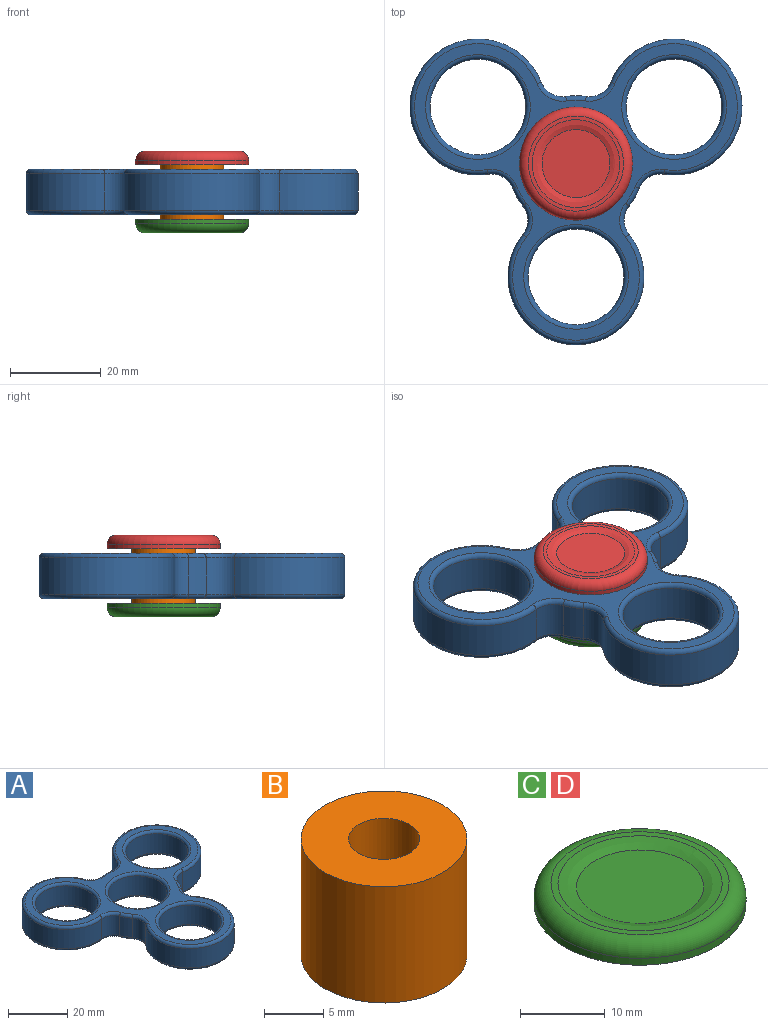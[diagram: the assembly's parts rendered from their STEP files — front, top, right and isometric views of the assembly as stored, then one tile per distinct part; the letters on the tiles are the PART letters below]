
ASSEMBLY  parts=4 mates=3
PART A: 50 faces, bbox 75.8x70x10 mm
  f0: cylinder r=15mm len=8mm, axis (0,0,-1), area 36.4mm2, adj f12,f17,f28,f39
  f1: cylinder r=15mm len=30mm, axis (0,0,-1), area 539mm2, adj f12,f13,f24,f35
  f2: cylinder r=15mm len=8mm, axis (0,0,-1), area 36.4mm2, adj f13,f14,f20,f31
  f3: cylinder r=15mm len=30mm, axis (0,0,-1), area 539mm2, adj f14,f15,f19,f32
  f4: cylinder r=15mm len=8mm, axis (0,0,-1), area 36.4mm2, adj f15,f16,f23,f36
  f5: cylinder r=10.56mm len=21.12mm, axis (0,0,-1), area 530.8mm2, adj f43,f48
  f6: cylinder r=10mm len=20mm, axis (0,0,-1), area 502.7mm2, adj f44,f47
  f7: cylinder r=15mm len=30mm, axis (0,0,-1), area 539mm2, adj f16,f17,f27,f40
  f8: cylinder r=10.56mm len=21.12mm, axis (0,0,-1), area 530.8mm2, adj f45,f46
  f9: cylinder r=10.56mm len=21.12mm, axis (0,0,-1), area 530.8mm2, adj f42,f49
  f10: plane 71.3x65.5mm, normal (0,0,1), area 795.3mm2, adj f18,f19,f20,f21,f22,f23,f24,f25
  f11: plane 71.3x65.5mm, normal (0,0,-1), area 795.3mm2, adj f30,f31,f32,f33,f34,f35,f36,f37
  f12: cylinder r=5mm len=8mm, axis (0,0,1), area 54mm2, adj f0,f1,f26,f37
  f13: cylinder r=5mm len=8mm, axis (0,0,1), area 54mm2, adj f1,f2,f22,f33
  f14: cylinder r=5mm len=8mm, axis (0,0,1), area 54mm2, adj f2,f3,f18,f30
  f15: cylinder r=5mm len=8mm, axis (0,0,1), area 54mm2, adj f3,f4,f21,f34
  f16: cylinder r=5mm len=8mm, axis (0,0,1), area 54mm2, adj f4,f7,f25,f38
  f17: cylinder r=5mm len=8mm, axis (0,0,1), area 54mm2, adj f0,f7,f29,f41
  f18: torus R=6mm, axis (0,0,1), area 11.4mm2, adj f10,f14,f19,f20
  f19: torus R=14mm, axis (0,0,1), area 103.3mm2, adj f3,f10,f18,f21
  f20: torus R=14mm, axis (0,0,1), area 7mm2, adj f2,f10,f18,f22
  f21: torus R=6mm, axis (0,0,1), area 11.4mm2, adj f10,f15,f19,f23
  f22: torus R=6mm, axis (0,0,1), area 11.4mm2, adj f10,f13,f20,f24
  f23: torus R=14mm, axis (0,0,1), area 7mm2, adj f4,f10,f21,f25
  f24: torus R=14mm, axis (0,0,1), area 103.3mm2, adj f1,f10,f22,f26
  f25: torus R=6mm, axis (0,0,1), area 11.4mm2, adj f10,f16,f23,f27
  f26: torus R=6mm, axis (0,0,1), area 11.4mm2, adj f10,f12,f24,f28
  f27: torus R=14mm, axis (0,0,1), area 103.3mm2, adj f7,f10,f25,f29
  f28: torus R=14mm, axis (0,0,1), area 7mm2, adj f0,f10,f26,f29
  f29: torus R=6mm, axis (0,0,1), area 11.4mm2, adj f10,f17,f27,f28
  f30: torus R=6mm, axis (0,0,1), area 11.4mm2, adj f11,f14,f31,f32
  f31: torus R=14mm, axis (0,0,1), area 7mm2, adj f2,f11,f30,f33
  f32: torus R=14mm, axis (0,0,1), area 103.3mm2, adj f3,f11,f30,f34
  f33: torus R=6mm, axis (0,0,1), area 11.4mm2, adj f11,f13,f31,f35
  f34: torus R=6mm, axis (0,0,1), area 11.4mm2, adj f11,f15,f32,f36
  f35: torus R=14mm, axis (0,0,1), area 103.3mm2, adj f1,f11,f33,f37
  f36: torus R=14mm, axis (0,0,1), area 7mm2, adj f4,f11,f34,f38
  f37: torus R=6mm, axis (0,0,1), area 11.4mm2, adj f11,f12,f35,f39
  f38: torus R=6mm, axis (0,0,1), area 11.4mm2, adj f11,f16,f36,f40
  f39: torus R=14mm, axis (0,0,1), area 7mm2, adj f0,f11,f37,f41
  f40: torus R=14mm, axis (0,0,1), area 103.3mm2, adj f7,f11,f38,f41
  f41: torus R=6mm, axis (0,0,1), area 11.4mm2, adj f11,f17,f39,f40
  f42: torus R=11.56mm, axis (0,0,1), area 107.8mm2, adj f9,f11
  f43: torus R=11.56mm, axis (0,0,1), area 107.8mm2, adj f5,f11
  f44: torus R=11mm, axis (0,0,1), area 102.3mm2, adj f6,f11
  f45: torus R=11.56mm, axis (0,0,1), area 107.8mm2, adj f8,f11
  f46: torus R=11.56mm, axis (0,0,1), area 107.8mm2, adj f8,f10
  f47: torus R=11mm, axis (0,0,1), area 102.3mm2, adj f6,f10
  f48: torus R=11.56mm, axis (0,0,1), area 107.8mm2, adj f5,f10
  f49: torus R=11.56mm, axis (0,0,1), area 107.8mm2, adj f9,f10
PART B: 4 faces, bbox 14x14x12 mm
  f0: cylinder r=7mm len=14mm, axis (0,0,-1), area 527.8mm2, adj f1,f2
  f1: plane 14x14mm, normal (0,0,1), area 125.7mm2, adj f0,f3
  f2: plane 14x14mm, normal (0,0,-1), area 125.7mm2, adj f0,f3
  f3: cylinder r=3mm len=12mm, axis (0,0,1), area 226.2mm2, adj f1,f2
PART C: 8 faces, bbox 27.1x27.1x9 mm
  f0: cylinder r=2.75mm len=6mm, axis (0,0,-1), area 103.7mm2, adj f1,f4
  f1: plane 5.5x5.5mm, normal (0,0,-1), area 23.8mm2, adj f0
  f2: cylinder r=12.5mm len=25mm, axis (0,0,-1), area 78.5mm2, adj f4,f7
  f3: plane 21.01x21.01mm, normal (0,0,1), area 52mm2, adj f6,f7
  f4: plane 25x25mm, normal (0,0,-1), area 467.1mm2, adj f0,f2
  f5: plane 15.01x15.01mm, normal (0,0,1), area 176.7mm2, adj f6
  f6: bspline ~19.36x19.36mm, area 121.5mm2, adj f3,f5
  f7: torus R=10.5mm, axis (0,0,1), area 232.4mm2, adj f2,f3
PART D: same geometry as C
PLACE A t=(-10.71,-1.96,-8.03)mm fixed
PLACE B t=(-10.71,-1.96,-9.03)mm
PLACE C rot(axis=(1,0,0),180deg) t=(-10.71,-1.96,-3.03)mm
PLACE D t=(-10.71,-1.96,-3.03)mm
MATE slider B.f0 <-> A.f4  axis (0,0,-1) through (-10.71,-1.96,-3.03)mm
MATE fastened D.f0 <-> B.f0  axis (0,0,-1) through (-10.71,-1.96,2.97)mm
MATE fastened C.f0 <-> B.f3  axis (0,0,1) through (-10.71,-1.96,-9.03)mm
